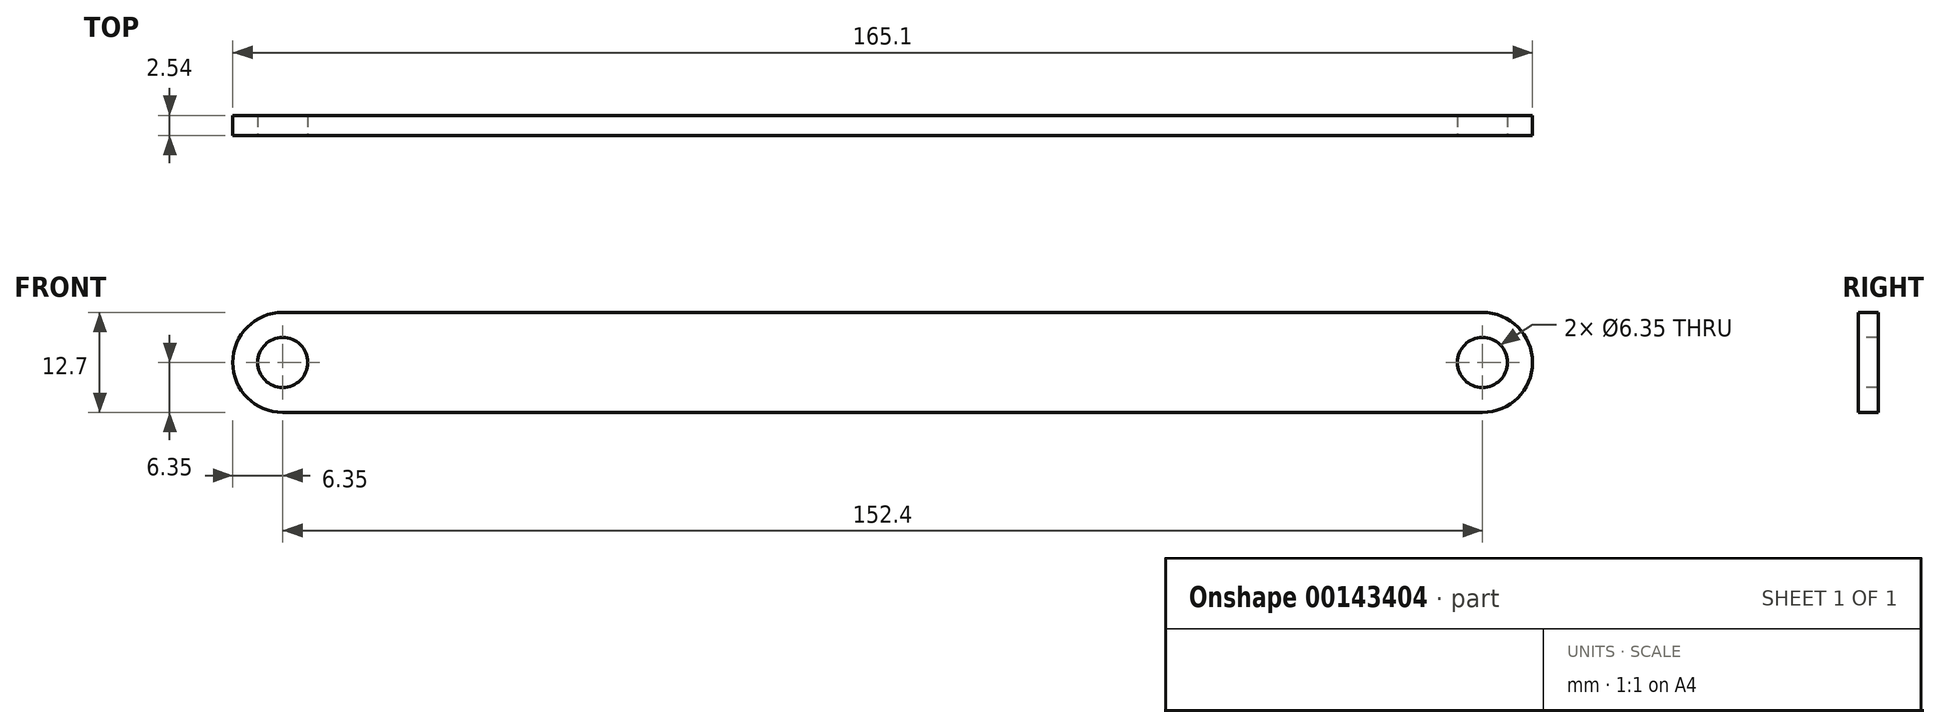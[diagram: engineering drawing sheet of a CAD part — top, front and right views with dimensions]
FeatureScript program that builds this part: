
annotation { "Feature Type Name" : "Feature", "Feature Type Description" : "" }
export const myFeature = defineFeature(function(context is Context, id is Id, definition is map)
    precondition{}
    {
        {
            var Q0;
            Q0=qCreatedBy(makeId("Front.planeOp"),FACE);
            var sketch = newSketch(context, id + "F0", { "sketchPlane" : qUnion([Q0])});
            skCircle(sketch, "E0", {"center": v(0, 0) * mm, "radius": 3.18 * mm});
            skArc(sketch, "E1", {"start": v(0, -6.35) * mm, "mid": v(6.35, 0) * mm, "end": v(0, 6.35) * mm});
            skLineSegment(sketch, "E2", {"start": v(0, 6.35) * mm, "end": v(-76.2, 6.35) * mm});
            skLineSegment(sketch, "E3", {"start": v(0, -6.35) * mm, "end": v(-76.2, -6.35) * mm});
            skLineSegment(sketch, "E4", {"start": v(-76.2, 6.35) * mm, "end": v(-76.2, -6.35) * mm});
            skSolve(sketch);
        }
        {
            var Q0;
            Q0=makeQuery(id+"F0.imprint","IMPRINT",FACE,{"disambiguationData":[TD([[makeQuery(id+"F0.imprint","IMPRINT",EDGE,{"derivedFrom":sQuery(id+"F0.wireOp",EDGE,"E0")}),-1.0]])]});
            extrude(context, id + "F1", {"entities" : qUnion([Q0]), "oppositeDirection" : true, "depth" : 2.54 * mm});
        }
        {
            var Q0;
            Q0=makeQuery(id+"F1.opExtrude","SWEPT_BODY",BODY,{"disambiguationData":[OSD([sQuery(id+"F0.wireOp",EDGE,"E0"),sQuery(id+"F0.wireOp",EDGE,"E1"),sQuery(id+"F0.wireOp",EDGE,"E2"),sQuery(id+"F0.wireOp",EDGE,"E3"),sQuery(id+"F0.wireOp",EDGE,"E4")])]});
            var Q1;
            Q1=makeQuery(id+"F1.opExtrude","SWEPT_FACE",FACE,{"disambiguationData":[OSD([sQuery(id+"F0.wireOp",EDGE,"E4")])]});
            mirror(context, id + "F2", {"operationType" : NewBodyOperationType.ADD, "entities" : qUnion([Q0]), "mirrorPlane" : qUnion([Q1])});
        }
    });
